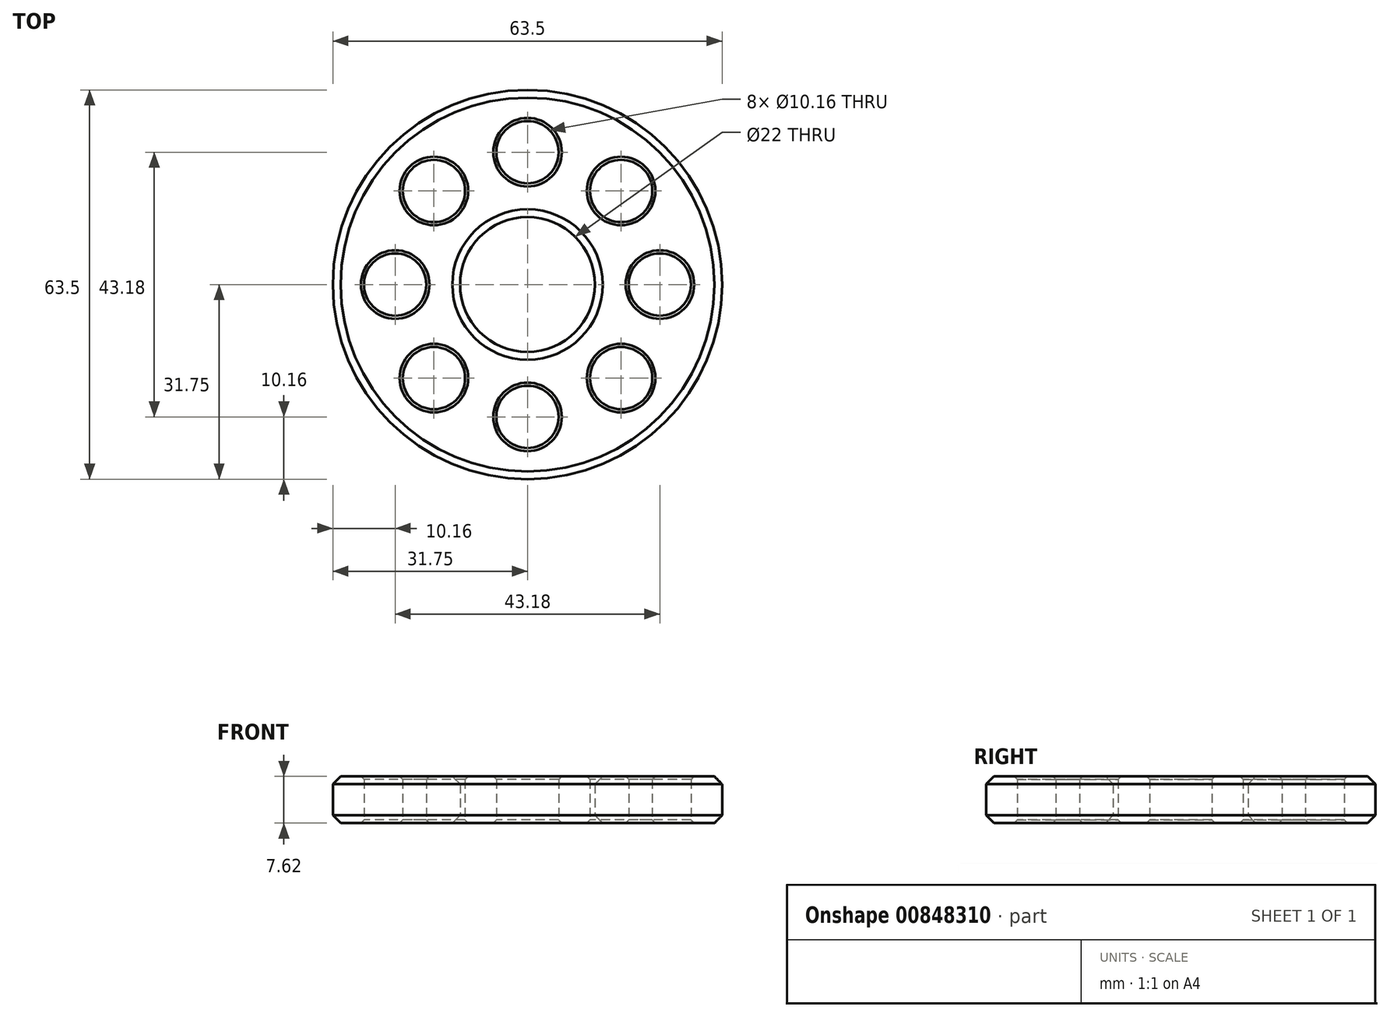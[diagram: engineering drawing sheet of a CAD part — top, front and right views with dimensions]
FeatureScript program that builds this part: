
annotation { "Feature Type Name" : "Feature", "Feature Type Description" : "" }
export const myFeature = defineFeature(function(context is Context, id is Id, definition is map)
    precondition{}
    {
        {
            var Q0;
            Q0=qCreatedBy(makeId("Top.planeOp"),FACE);
            var sketch = newSketch(context, id + "F0", { "sketchPlane" : qUnion([Q0])});
            skCircle(sketch, "E0", {"center": v(0, 0) * mm, "radius": 31.75 * mm});
            skCircle(sketch, "E1", {"center": v(0, 0) * mm, "radius": 11 * mm});
            skCircle(sketch, "E2", {"center": v(0, 0) * mm, "radius": 21.59 * mm, "construction": true});
            skCircle(sketch, "E3", {"center": v(-21.59, 0) * mm, "radius": 5.08 * mm});
            skCircle(sketch, "E4.1.0", {"center": v(-15.27, -15.27) * mm, "radius": 5.08 * mm});
            skCircle(sketch, "E4.2.0", {"center": v(0, -21.59) * mm, "radius": 5.08 * mm});
            skCircle(sketch, "E4.3.0", {"center": v(15.27, -15.27) * mm, "radius": 5.08 * mm});
            skCircle(sketch, "E4.4.0", {"center": v(21.59, 0) * mm, "radius": 5.08 * mm});
            skCircle(sketch, "E4.5.0", {"center": v(15.27, 15.27) * mm, "radius": 5.08 * mm});
            skCircle(sketch, "E4.6.0", {"center": v(0, 21.59) * mm, "radius": 5.08 * mm});
            skCircle(sketch, "E4.7.0", {"center": v(-15.27, 15.27) * mm, "radius": 5.08 * mm});
            skSolve(sketch);
        }
        {
            var Q0;
            Q0=makeQuery(id+"F0.imprint","IMPRINT",FACE,{"disambiguationData":[TD([[makeQuery(id+"F0.imprint","IMPRINT",EDGE,{"derivedFrom":sQuery(id+"F0.wireOp",EDGE,"E0")}),1.0]])]});
            extrude(context, id + "F1", {"entities" : qUnion([Q0]), "depth" : 7.62 * mm, "offsetDistance" : 25.4 * mm});
        }
        {
            var Q0;
            Q0=makeQuery(id+"F1.opExtrude","CAP_EDGE",EDGE,{"disambiguationData":[OSD([sQuery(id+"F0.wireOp",EDGE,"E0")])],"isStart":false});
            var Q1;
            Q1=makeQuery(id+"F1.opExtrude","CAP_EDGE",EDGE,{"disambiguationData":[OSD([sQuery(id+"F0.wireOp",EDGE,"E1")])],"isStart":false});
            chamfer(context, id + "F2", {"entities" : qUnion([Q0, Q1]), "width" : 1.27 * mm, "tangentPropagation" : true});
        }
        {
            var Q0;
            Q0=makeQuery(id+"F1.opExtrude","CAP_EDGE",EDGE,{"disambiguationData":[OSD([sQuery(id+"F0.wireOp",EDGE,"E0")])],"isStart":true});
            var Q1;
            Q1=makeQuery(id+"F1.opExtrude","CAP_EDGE",EDGE,{"disambiguationData":[OSD([sQuery(id+"F0.wireOp",EDGE,"E1")])],"isStart":true});
            chamfer(context, id + "F3", {"entities" : qUnion([Q0, Q1]), "width" : 1.27 * mm, "tangentPropagation" : true});
        }
        {
            var Q0;
            Q0=makeQuery(id+"F1.opExtrude","CAP_EDGE",EDGE,{"disambiguationData":[OSD([sQuery(id+"F0.wireOp",EDGE,"E4.2.0")])],"isStart":true});
            var Q1;
            Q1=makeQuery(id+"F1.opExtrude","SWEPT_FACE",FACE,{"disambiguationData":[OSD([sQuery(id+"F0.wireOp",EDGE,"E4.3.0")])]});
            var Q2;
            Q2=makeQuery(id+"F1.opExtrude","SWEPT_FACE",FACE,{"disambiguationData":[OSD([sQuery(id+"F0.wireOp",EDGE,"E4.2.0")])]});
            var Q3;
            Q3=makeQuery(id+"F1.opExtrude","SWEPT_FACE",FACE,{"disambiguationData":[OSD([sQuery(id+"F0.wireOp",EDGE,"E4.1.0")])]});
            var Q4;
            Q4=makeQuery(id+"F1.opExtrude","SWEPT_FACE",FACE,{"disambiguationData":[OSD([sQuery(id+"F0.wireOp",EDGE,"E3")])]});
            var Q5;
            Q5=makeQuery(id+"F1.opExtrude","SWEPT_FACE",FACE,{"disambiguationData":[OSD([sQuery(id+"F0.wireOp",EDGE,"E4.7.0")])]});
            var Q6;
            Q6=makeQuery(id+"F1.opExtrude","SWEPT_FACE",FACE,{"disambiguationData":[OSD([sQuery(id+"F0.wireOp",EDGE,"E4.6.0")])]});
            var Q7;
            Q7=makeQuery(id+"F1.opExtrude","SWEPT_FACE",FACE,{"disambiguationData":[OSD([sQuery(id+"F0.wireOp",EDGE,"E4.5.0")])]});
            var Q8;
            Q8=makeQuery(id+"F1.opExtrude","CAP_EDGE",EDGE,{"disambiguationData":[OSD([sQuery(id+"F0.wireOp",EDGE,"E4.4.0")])],"isStart":true});
            var Q9;
            Q9=makeQuery(id+"F1.opExtrude","SWEPT_FACE",FACE,{"disambiguationData":[OSD([sQuery(id+"F0.wireOp",EDGE,"E4.4.0")])]});
            chamfer(context, id + "F4", {"entities" : qUnion([Q0, Q1, Q2, Q3, Q4, Q5, Q6, Q7, Q8, Q9]), "width" : 0.5 * mm, "tangentPropagation" : true});
        }
    });
